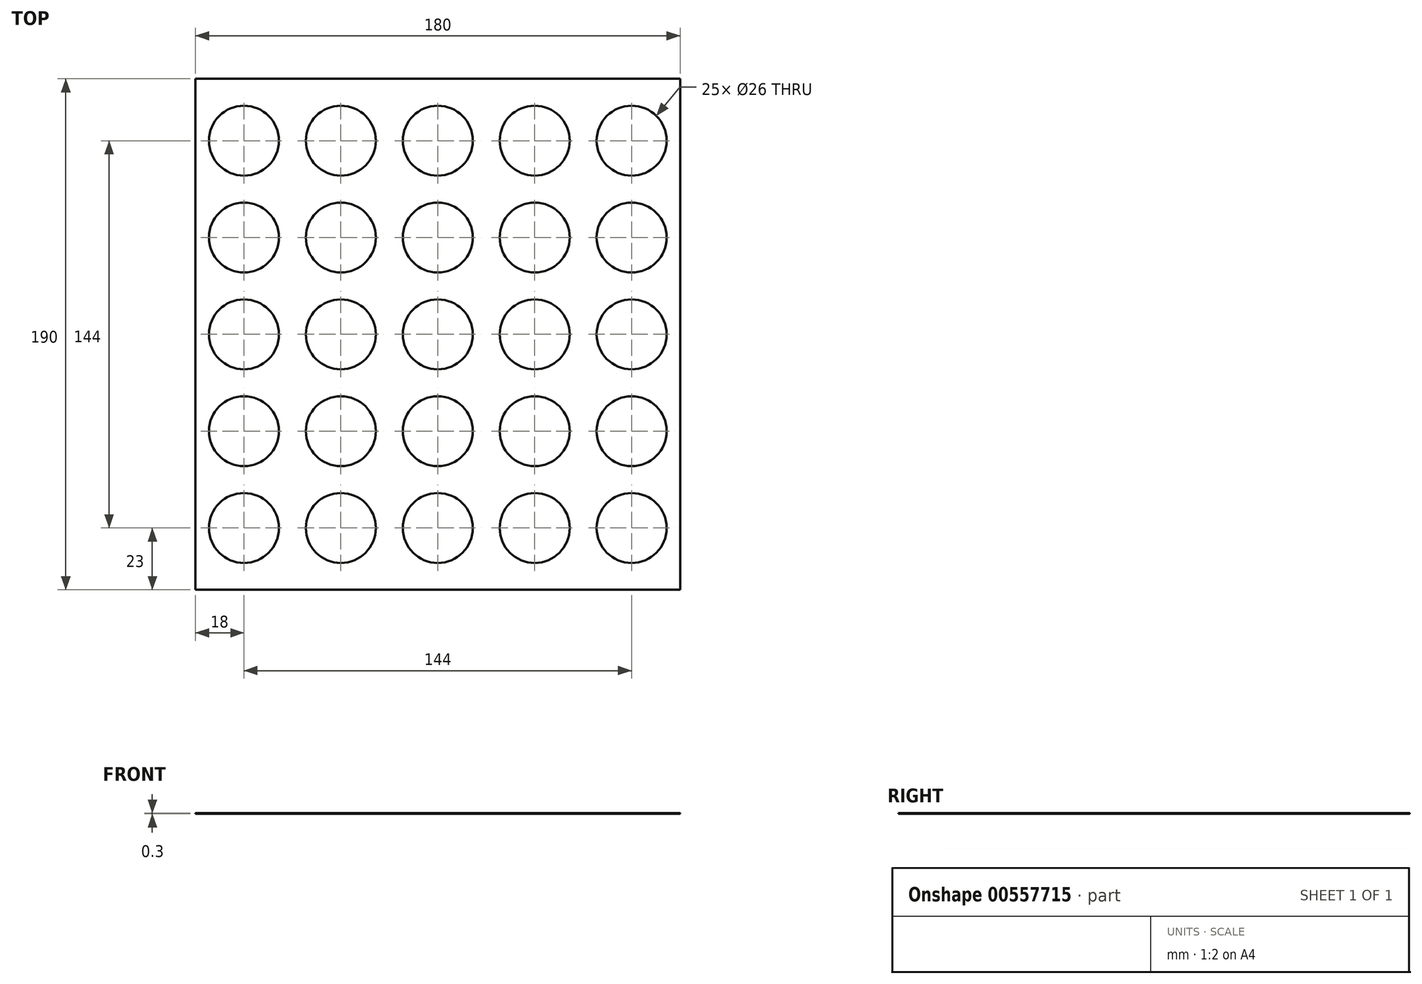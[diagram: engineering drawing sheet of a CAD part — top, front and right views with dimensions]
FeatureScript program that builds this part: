
annotation { "Feature Type Name" : "Feature", "Feature Type Description" : "" }
export const myFeature = defineFeature(function(context is Context, id is Id, definition is map)
    precondition{}
    {
        {
            var Q0;
            Q0=qCreatedBy(makeId("Top.planeOp"),FACE);
            var sketch = newSketch(context, id + "F0", { "sketchPlane" : qUnion([Q0])});
            skCircle(sketch, "E0", {"center": v(0, 0) * mm, "radius": 13 * mm});
            skCircle(sketch, "E1.0.1.0", {"center": v(0, 36) * mm, "radius": 13 * mm});
            skCircle(sketch, "E1.0.2.0", {"center": v(0, 72) * mm, "radius": 13 * mm});
            skCircle(sketch, "E1.0.3.0", {"center": v(0, 108) * mm, "radius": 13 * mm});
            skCircle(sketch, "E1.0.4.0", {"center": v(0, 144) * mm, "radius": 13 * mm});
            skCircle(sketch, "E1.1.0.0", {"center": v(36, 0) * mm, "radius": 13 * mm});
            skCircle(sketch, "E1.1.1.0", {"center": v(36, 36) * mm, "radius": 13 * mm});
            skCircle(sketch, "E1.1.2.0", {"center": v(36, 72) * mm, "radius": 13 * mm});
            skCircle(sketch, "E1.1.3.0", {"center": v(36, 108) * mm, "radius": 13 * mm});
            skCircle(sketch, "E1.1.4.0", {"center": v(36, 144) * mm, "radius": 13 * mm});
            skCircle(sketch, "E1.2.0.0", {"center": v(72, 0) * mm, "radius": 13 * mm});
            skCircle(sketch, "E1.2.1.0", {"center": v(72, 36) * mm, "radius": 13 * mm});
            skCircle(sketch, "E1.2.2.0", {"center": v(72, 72) * mm, "radius": 13 * mm});
            skCircle(sketch, "E1.2.3.0", {"center": v(72, 108) * mm, "radius": 13 * mm});
            skCircle(sketch, "E1.2.4.0", {"center": v(72, 144) * mm, "radius": 13 * mm});
            skCircle(sketch, "E1.3.0.0", {"center": v(108, 0) * mm, "radius": 13 * mm});
            skCircle(sketch, "E1.3.1.0", {"center": v(108, 36) * mm, "radius": 13 * mm});
            skCircle(sketch, "E1.3.2.0", {"center": v(108, 72) * mm, "radius": 13 * mm});
            skCircle(sketch, "E1.3.3.0", {"center": v(108, 108) * mm, "radius": 13 * mm});
            skCircle(sketch, "E1.3.4.0", {"center": v(108, 144) * mm, "radius": 13 * mm});
            skCircle(sketch, "E1.4.0.0", {"center": v(144, 0) * mm, "radius": 13 * mm});
            skCircle(sketch, "E1.4.1.0", {"center": v(144, 36) * mm, "radius": 13 * mm});
            skCircle(sketch, "E1.4.2.0", {"center": v(144, 72) * mm, "radius": 13 * mm});
            skCircle(sketch, "E1.4.3.0", {"center": v(144, 108) * mm, "radius": 13 * mm});
            skCircle(sketch, "E1.4.4.0", {"center": v(144, 144) * mm, "radius": 13 * mm});
            skLineSegment(sketch, "E1.direction1", {"start": v(0, 0) * mm, "end": v(36, 0) * mm, "construction": true});
            skLineSegment(sketch, "E1.direction2", {"start": v(0, 0) * mm, "end": v(0, 36) * mm, "construction": true});
            skLineSegment(sketch, "E2.bottom", {"start": v(-18, -23) * mm, "end": v(162, -23) * mm});
            skLineSegment(sketch, "E2.top", {"start": v(-18, 167) * mm, "end": v(162, 167) * mm});
            skLineSegment(sketch, "E2.left", {"start": v(-18, -23) * mm, "end": v(-18, 167) * mm});
            skLineSegment(sketch, "E2.right", {"start": v(162, -23) * mm, "end": v(162, 167) * mm});
            skSolve(sketch);
        }
        {
            var Q0;
            Q0=makeQuery(id+"F0.imprint","IMPRINT",FACE,{"disambiguationData":[TD([[makeQuery(id+"F0.imprint","IMPRINT",EDGE,{"derivedFrom":sQuery(id+"F0.wireOp",EDGE,"E0")}),-1.0]])]});
            extrude(context, id + "F1", {"entities" : qUnion([Q0]), "depth" : 0.3 * mm, "offsetDistance" : 25 * mm});
        }
    });
